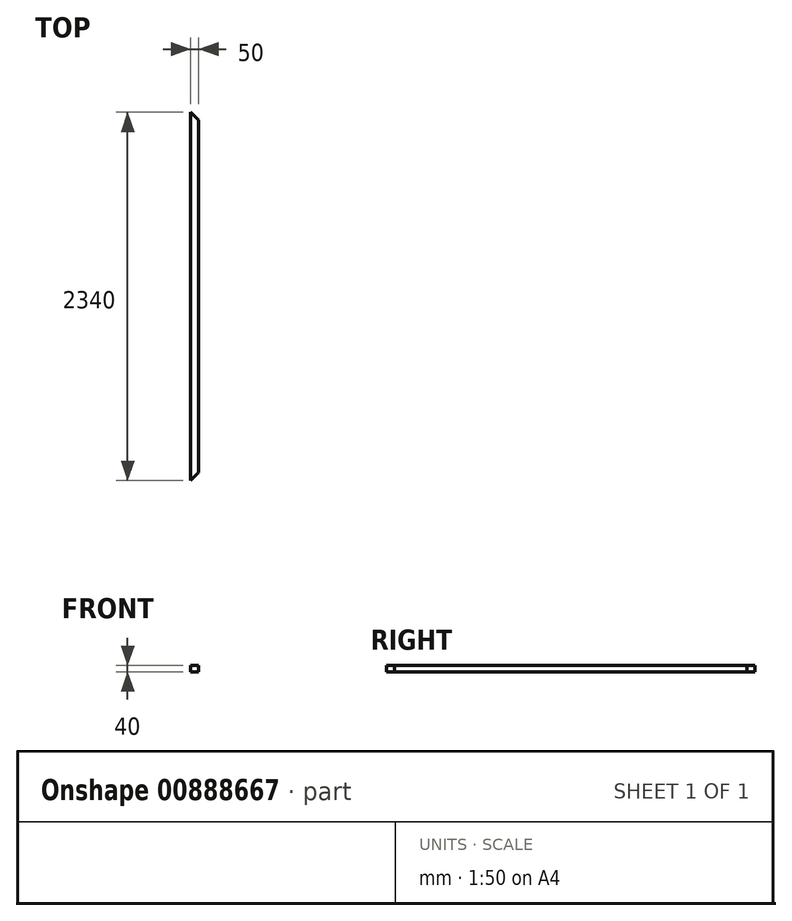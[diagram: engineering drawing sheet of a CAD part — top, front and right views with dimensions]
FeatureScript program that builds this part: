
annotation { "Feature Type Name" : "Feature", "Feature Type Description" : "" }
export const myFeature = defineFeature(function(context is Context, id is Id, definition is map)
    precondition{}
    {
        {
            var Q0;
            Q0=qCreatedBy(makeId("Front.planeOp"),FACE);
            var sketch = newSketch(context, id + "F0", { "sketchPlane" : qUnion([Q0])});
            skLineSegment(sketch, "E0.bottom", {"start": v(0, 0) * mm, "end": v(50, 0) * mm});
            skLineSegment(sketch, "E0.top", {"start": v(0, 40) * mm, "end": v(50, 40) * mm});
            skLineSegment(sketch, "E0.left", {"start": v(0, 0) * mm, "end": v(0, 40) * mm});
            skLineSegment(sketch, "E0.right", {"start": v(50, 0) * mm, "end": v(50, 40) * mm});
            skSolve(sketch);
        }
        {
            var Q0;
            Q0=makeQuery(id+"F0.imprint","IMPRINT",FACE,{"disambiguationData":[TD([[makeQuery(id+"F0.imprint","IMPRINT",EDGE,{"derivedFrom":sQuery(id+"F0.wireOp",EDGE,"E0.bottom")}),1.0]])]});
            extrude(context, id + "F1", {"entities" : qUnion([Q0]), "depth" : 2340 * mm, "offsetDistance" : 25 * mm});
        }
        {
            var Q0;
            Q0=makeQuery(id+"F1.opExtrude","CAP_EDGE",EDGE,{"disambiguationData":[OSD([sQuery(id+"F0.wireOp",EDGE,"E0.right")])],"isStart":true});
            var Q1;
            Q1=makeQuery(id+"F1.opExtrude","CAP_EDGE",EDGE,{"disambiguationData":[OSD([sQuery(id+"F0.wireOp",EDGE,"E0.right")])],"isStart":false});
            chamfer(context, id + "F2", {"entities" : qUnion([Q0, Q1]), "chamferType" : ChamferType.OFFSET_ANGLE, "width" : 50 * mm, "oppositeDirection" : false, "angle" : 45 * degree, "tangentPropagation" : true});
        }
    });
